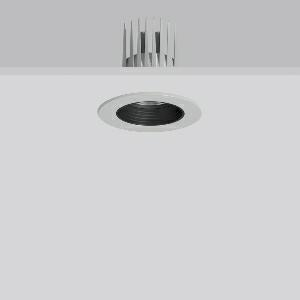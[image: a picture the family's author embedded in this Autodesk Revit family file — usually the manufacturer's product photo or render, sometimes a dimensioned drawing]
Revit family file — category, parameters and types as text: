
# Revit family: heledon_mini_e_901744_004_3_4bb7
name_source: partatom
category: Lighting Fixtures
units: mm (PartAtom-declared; Revit-internal decimal feet)

## family parameters
Cut with Voids When Loaded = No
Host = Face
Light Source = No
Part Type = Normal
Room Calculation Point = No
Round Connector Dimension = Use Diameter
Shared = No

## types (1)
- HELEDON mini E (1 x LED Modul 935, 2150 lm, 3500)
    Apparent Load = 20 VA
    Approval mark = CE
    CIE Flux Codes = 96 100 100 100 100
    Color Rendering = 92
    Color Temperature = 3500
    Default Elevation = 1800 mm
    Description = Series: HELEDON mini
Round recessed downlight. Housing: die-cast aluminium, powder-coated. Black plastic ring and recessed LED to prevent glare from the side. Optical assembly with lens made of plastic (polycarbonate) for the best homogeneous light distribution - can be changed without tools. Best colour rendering index Ra>90. Suitable for Recessed ceiling mounting. Installation without tools thanks to spring fastening system. Including separate LED converter with connecting cable 600 mm.High quality converter without flickering and stroboscopic effect. Through-wiring box (5 pole) available as accessory. The following accessories can be mounted without use of tools: interchangeable lenses, decorative glasses, honeycomb louvre, clear and frosted diffusers, white interchangeable plastic ring. 
Colour: silver
Diameter: 124 mm
Height: 3 mm
Cut-out diameter: 114 mm
Recess height: 170 mm
Luminaire: recess height: 120 mm
Lamp: LED
Socket: without socket
Colour temperature: 3500K
Colour rendering index (CRI): 92
System power: 20 W
Rated luminous flux: 2150 lm
Luminous efficiency: 108 lm/W
Control gear: Regulated power supply
Protection class: II
Type of protection: IP 20
    Height = 0 mm  [stored 0 ft]
    Lamp = 1 x LED Modul 935
    Lamp Light Flux = 2150 lm
    Lamp count = 1
    Length = 124 mm  [stored 0.406824 ft]
    Lifetime = 50000 h
    Luminous efficacy = 108 lm/W
    Manufacturer = RZB
    ModVariant = No
    Model = 901744.004.3
    Mounting Place = Ceiling
    Mounting Type = Recessed
    Number of Poles = 1
    OnlyDefault = Yes
    Power Factor = 1
    Product Name = HELEDON mini E
    Product group = Recessed downlights
    ProductGroupID = 402
    Protection Class = Protection class II
    Protection Degree = IP 20
    RLX_Detail_Level = 1
    RLX_Emergency_Light_Flux = 0 lm
    RLX_Emergency_Type = 0
    RLX_Emergency_Type_DB = No
    RlxData = <blob elided: 124765 chars, md5=2a81df47>
    Socket = socket
    Standby Power = 0 W
    System Light Flux = 2150 lm
    System Power = 20 W
    Type Comments = Product without accessories
    Type Image = 901656.004.jpg
    URL = http://relux.com
    VarID = ---
    Voltage = 230 V
    Voltage Range = 220-240 V
    Weight = 0.00 kg
    Width = 0 mm  [stored 0 ft]

note: [stored X ft] marks values corroborated as IEEE doubles in the binary element streams (Revit-internal decimal feet)

## geometry (parser evidence)
native form markers: Blend x4, Sweep x11
no freeform markers — native parametric forms only
